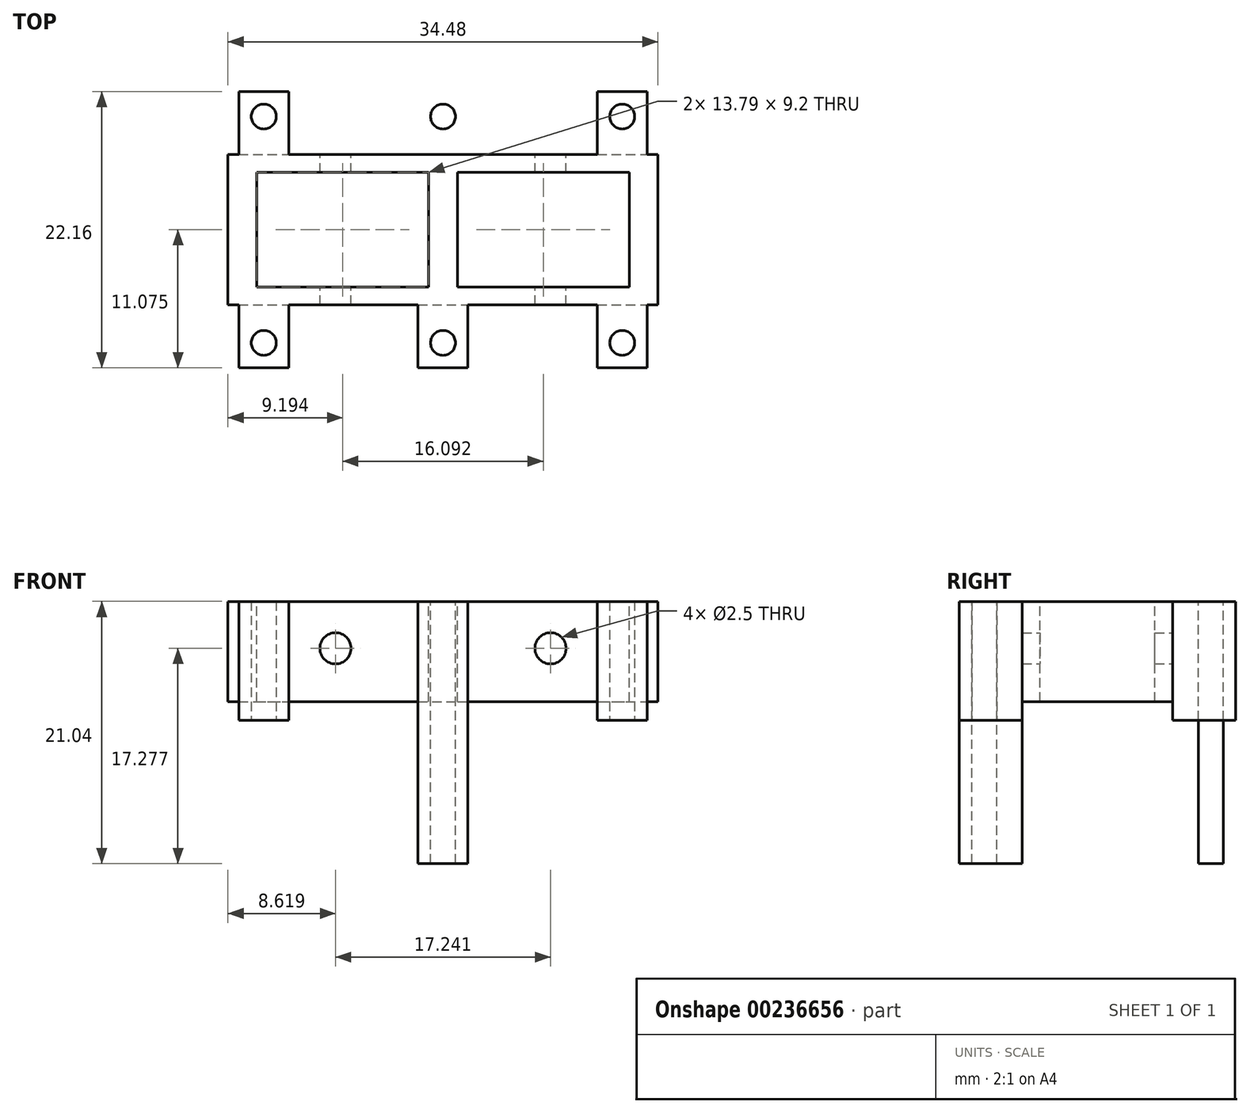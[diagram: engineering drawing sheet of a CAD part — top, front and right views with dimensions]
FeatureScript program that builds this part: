
annotation { "Feature Type Name" : "Feature", "Feature Type Description" : "" }
export const myFeature = defineFeature(function(context is Context, id is Id, definition is map)
    precondition{}
    {
        {
            assignVariable(context, id + "F0", {"name" : "scale", "anyValue" : 1 / 87});
        }
        {
            var Q0;
            Q0=qCreatedBy(makeId("Front.planeOp"),FACE);
            var sketch = newSketch(context, id + "F1", { "sketchPlane" : qUnion([Q0])});
            skLineSegment(sketch, "E0", {"start": v(0, 0) * mm, "end": v(17.24, 0) * mm});
            skLineSegment(sketch, "E1", {"start": v(17.24, 0) * mm, "end": v(17.24, 1.72) * mm});
            skLineSegment(sketch, "E2", {"start": v(17.24, 8.05) * mm, "end": v(0, 8.05) * mm});
            skLineSegment(sketch, "E3", {"start": v(0, 8.05) * mm, "end": v(0, 0) * mm, "construction": true});
            skLineSegment(sketch, "E4", {"start": v(14.37, 1.72) * mm, "end": v(14.37, 0) * mm, "construction": true});
            skLineSegment(sketch, "E5", {"start": v(0, -1.5) * mm, "end": v(17.24, -1.5) * mm, "construction": true});
            skLineSegment(sketch, "E6", {"start": v(17.24, -1.5) * mm, "end": v(17.24, 0) * mm, "construction": true});
            skLineSegment(sketch, "E7", {"start": v(17.24, 1.72) * mm, "end": v(0, 1.72) * mm, "construction": true});
            skCircle(sketch, "E8", {"center": v(8.62, 4.29) * mm, "radius": 5.78 * mm, "construction": true});
            skPoint(sketch, "E9", {"position": v(8.62, 1.72) * mm});
            skPoint(sketch, "E10.MirrorP", {"position": v(-8.62, 1.72) * mm});
            skLineSegment(sketch, "E11.MirrorCS", {"start": v(0, 0) * mm, "end": v(-17.24, 0) * mm});
            skCircle(sketch, "E12.MirrorC", {"center": v(-8.62, 4.29) * mm, "radius": 5.78 * mm, "construction": true});
            skLineSegment(sketch, "E13.MirrorCS", {"start": v(-14.37, 1.72) * mm, "end": v(-14.37, 0) * mm, "construction": true});
            skLineSegment(sketch, "E14.MirrorCS", {"start": v(-17.24, -1.5) * mm, "end": v(-17.24, 0) * mm, "construction": true});
            skLineSegment(sketch, "E15.MirrorCS", {"start": v(-17.24, 0) * mm, "end": v(-17.24, 1.72) * mm});
            skLineSegment(sketch, "E16.MirrorCS", {"start": v(-17.24, 8.05) * mm, "end": v(0, 8.05) * mm});
            skLineSegment(sketch, "E17.MirrorCS", {"start": v(0, -1.5) * mm, "end": v(-17.24, -1.5) * mm, "construction": true});
            skLineSegment(sketch, "E18.MirrorCS", {"start": v(-17.24, 1.72) * mm, "end": v(0, 1.72) * mm, "construction": true});
            skCircle(sketch, "E19", {"center": v(8.62, 4.29) * mm, "radius": 1.25 * mm});
            skCircle(sketch, "E20", {"center": v(-8.62, 4.29) * mm, "radius": 1.25 * mm});
            skLineSegment(sketch, "E21", {"start": v(17.24, 1.72) * mm, "end": v(17.24, 8.05) * mm});
            skLineSegment(sketch, "E22", {"start": v(-17.24, 8.05) * mm, "end": v(-17.24, 1.72) * mm});
            skSolve(sketch);
        }
        {
            var Q0;
            Q0=qSketchRegion(id+"F1",true);
            extrude(context, id + "F2", {"entities" : qUnion([Q0]), "depth" : (1050 * getVariable(context, 'scale')) * mm});
        }
        {
            var Q0;
            Q0=makeQuery(id+"F2.opExtrude","SWEPT_FACE",FACE,{"disambiguationData":[OSD([sQuery(id+"F1.wireOp",EDGE,"E2"),sQuery(id+"F1.wireOp",EDGE,"E16.MirrorCS")])]});
            var sketch = newSketch(context, id + "F3", { "sketchPlane" : qUnion([Q0])});
            skLineSegment(sketch, "E23.bottom", {"start": v(-17.24, 0) * mm, "end": v(17.24, 0) * mm, "construction": true});
            skLineSegment(sketch, "E23.top", {"start": v(-17.24, -12.07) * mm, "end": v(17.24, -12.07) * mm, "construction": true});
            skLineSegment(sketch, "E23.left", {"start": v(-17.24, 0) * mm, "end": v(-17.24, -12.07) * mm, "construction": true});
            skLineSegment(sketch, "E23.right", {"start": v(17.24, 0) * mm, "end": v(17.24, -12.07) * mm, "construction": true});
            skLineSegment(sketch, "E24", {"start": v(-17.24, -1.44) * mm, "end": v(17.24, -1.44) * mm, "construction": true});
            skLineSegment(sketch, "E25", {"start": v(17.24, -1.44) * mm, "end": v(17.24, -10.63) * mm, "construction": true});
            skLineSegment(sketch, "E26", {"start": v(17.24, -10.63) * mm, "end": v(-17.24, -10.63) * mm, "construction": true});
            skLineSegment(sketch, "E27", {"start": v(-14.94, 0) * mm, "end": v(-14.94, -12.07) * mm, "construction": true});
            skLineSegment(sketch, "E28", {"start": v(14.94, 0) * mm, "end": v(14.94, -12.07) * mm, "construction": true});
            skLineSegment(sketch, "E29", {"start": v(-14.94, -1.44) * mm, "end": v(-1.15, -1.44) * mm});
            skLineSegment(sketch, "E30", {"start": v(-1.15, -1.44) * mm, "end": v(-1.15, -10.63) * mm});
            skLineSegment(sketch, "E31", {"start": v(-1.15, -10.63) * mm, "end": v(-14.94, -10.63) * mm});
            skLineSegment(sketch, "E32", {"start": v(-14.94, -10.63) * mm, "end": v(-14.94, -1.44) * mm});
            skLineSegment(sketch, "E33", {"start": v(1.15, -1.44) * mm, "end": v(14.94, -1.44) * mm});
            skLineSegment(sketch, "E34", {"start": v(14.94, -1.44) * mm, "end": v(14.94, -10.63) * mm});
            skLineSegment(sketch, "E35", {"start": v(14.94, -10.63) * mm, "end": v(1.15, -10.63) * mm});
            skLineSegment(sketch, "E36", {"start": v(0, 0) * mm, "end": v(0, -12.07) * mm, "construction": true});
            skLineSegment(sketch, "E37", {"start": v(1.15, -1.44) * mm, "end": v(1.15, -10.63) * mm});
            skLineSegment(sketch, "E38", {"start": v(1.15, -6.03) * mm, "end": v(-1.15, -6.03) * mm, "construction": true});
            skPoint(sketch, "E39", {"position": v(0, -6.03) * mm});
            skSolve(sketch);
        }
        {
            var Q0;
            Q0=qSketchRegion(id+"F3",true);
            extrude(context, id + "F4", {"entities" : qUnion([Q0]), "operationType" : NewBodyOperationType.REMOVE, "endBound" : BoundingType.THROUGH_ALL, "oppositeDirection" : true, "depth" : 25 * mm});
        }
        {
            var Q0;
            Q0=makeQuery(id+"F2.opExtrude","SWEPT_FACE",FACE,{"disambiguationData":[OSD([sQuery(id+"F1.wireOp",EDGE,"E0"),sQuery(id+"F1.wireOp",EDGE,"E11.MirrorCS")])]});
            var sketch = newSketch(context, id + "F5", { "sketchPlane" : qUnion([Q0])});
            skLineSegment(sketch, "E40.bottom", {"start": v(-50, 10.92) * mm, "end": v(50, 10.92) * mm, "construction": true});
            skLineSegment(sketch, "E40.top", {"start": v(-50, 1.15) * mm, "end": v(50, 1.15) * mm, "construction": true});
            skLineSegment(sketch, "E40.left", {"start": v(-50, 10.92) * mm, "end": v(-50, 1.15) * mm, "construction": true});
            skLineSegment(sketch, "E40.right", {"start": v(50, 10.92) * mm, "end": v(50, 1.15) * mm, "construction": true});
            skPoint(sketch, "E40.middle", {"position": v(0, 6.03) * mm});
            skPoint(sketch, "E40.middle.positionSnap0", {"position": v(1.15, 6.03) * mm});
            skPoint(sketch, "E40.centerSnap0", {"position": v(1.15, 6.03) * mm});
            skCircle(sketch, "E41", {"center": v(-14.37, 15.11) * mm, "radius": 4.2 * mm, "construction": true});
            skCircle(sketch, "E42", {"center": v(14.37, 15.11) * mm, "radius": 4.2 * mm, "construction": true});
            skCircle(sketch, "E43", {"center": v(-14.37, -3.05) * mm, "radius": 4.2 * mm, "construction": true});
            skCircle(sketch, "E44", {"center": v(14.37, -3.05) * mm, "radius": 4.2 * mm, "construction": true});
            skLineSegment(sketch, "E45", {"start": v(14.37, 15.11) * mm, "end": v(-14.37, 15.11) * mm, "construction": true});
            skLineSegment(sketch, "E46", {"start": v(-14.37, -3.05) * mm, "end": v(-14.37, 15.11) * mm, "construction": true});
            skLineSegment(sketch, "E47", {"start": v(14.37, 15.11) * mm, "end": v(14.37, -3.05) * mm, "construction": true});
            skLineSegment(sketch, "E48", {"start": v(-14.37, -3.05) * mm, "end": v(14.37, -3.05) * mm, "construction": true});
            skLineSegment(sketch, "E49", {"start": v(0, 15.11) * mm, "end": v(0, -3.05) * mm, "construction": true});
            skCircle(sketch, "E50", {"center": v(-14.37, -3.05) * mm, "radius": 1 * mm});
            skLineSegment(sketch, "E51", {"start": v(-17.24, 6.03) * mm, "end": v(17.24, 6.03) * mm, "construction": true});
            skLineSegment(sketch, "E52.MirrorCS", {"start": v(14.37, -3.05) * mm, "end": v(-14.37, -3.05) * mm, "construction": true});
            skCircle(sketch, "E53.MirrorC", {"center": v(14.37, -3.05) * mm, "radius": 1 * mm});
            skCircle(sketch, "E54.MirrorC", {"center": v(-14.37, 15.11) * mm, "radius": 1 * mm});
            skCircle(sketch, "E55.MirrorC", {"center": v(14.37, 15.11) * mm, "radius": 1 * mm});
            skLineSegment(sketch, "E56.bottom", {"start": v(-16.37, 12.07) * mm, "end": v(-12.37, 12.07) * mm});
            skLineSegment(sketch, "E56.top", {"start": v(-16.37, 17.11) * mm, "end": v(-12.37, 17.11) * mm});
            skLineSegment(sketch, "E56.left", {"start": v(-16.37, 12.07) * mm, "end": v(-16.37, 17.11) * mm});
            skLineSegment(sketch, "E56.right", {"start": v(-12.37, 12.07) * mm, "end": v(-12.37, 17.11) * mm});
            skPoint(sketch, "E57", {"position": v(-14.37, 12.07) * mm});
            skLineSegment(sketch, "E58.bottom", {"start": v(12.37, 12.07) * mm, "end": v(16.37, 12.07) * mm});
            skLineSegment(sketch, "E58.top", {"start": v(12.37, 17.11) * mm, "end": v(16.37, 17.11) * mm});
            skLineSegment(sketch, "E58.left", {"start": v(12.37, 12.07) * mm, "end": v(12.37, 17.11) * mm});
            skLineSegment(sketch, "E58.right", {"start": v(16.37, 12.07) * mm, "end": v(16.37, 17.11) * mm});
            skPoint(sketch, "E59", {"position": v(14.37, 12.07) * mm});
            skLineSegment(sketch, "E60.MirrorCS", {"start": v(-16.37, 0) * mm, "end": v(-16.37, -5.05) * mm});
            skLineSegment(sketch, "E61.MirrorCS", {"start": v(-16.37, 0) * mm, "end": v(-12.37, 0) * mm});
            skLineSegment(sketch, "E62.MirrorCS", {"start": v(-12.37, 0) * mm, "end": v(-12.37, -5.05) * mm});
            skLineSegment(sketch, "E63.MirrorCS", {"start": v(-16.37, -5.05) * mm, "end": v(-12.37, -5.05) * mm});
            skLineSegment(sketch, "E64.MirrorCS", {"start": v(12.37, 0) * mm, "end": v(16.37, 0) * mm});
            skLineSegment(sketch, "E65.MirrorCS", {"start": v(12.37, 0) * mm, "end": v(12.37, -5.05) * mm});
            skLineSegment(sketch, "E66.MirrorCS", {"start": v(12.37, -5.05) * mm, "end": v(16.37, -5.05) * mm});
            skLineSegment(sketch, "E67.MirrorCS", {"start": v(16.37, 0) * mm, "end": v(16.37, -5.05) * mm});
            skSolve(sketch);
        }
        {
            var Q0;
            Q0=qSketchRegion(id+"F5",true);
            var Q1;
            Q1=qConstructionFilter(qBodyType(qCreatedBy(id+"F5",EDGE),BodyType.WIRE),ConstructionObject.NO);
            var Q2;
            Q2=makeQuery(id+"F2.opExtrude","SWEPT_FACE",FACE,{"disambiguationData":[OSD([sQuery(id+"F1.wireOp",EDGE,"E2"),sQuery(id+"F1.wireOp",EDGE,"E16.MirrorCS")])]});
            extrude(context, id + "F6", {"entities" : qUnion([Q0]), "operationType" : NewBodyOperationType.ADD, "surfaceEntities" : qUnion([Q1]), "endBound" : BoundingType.UP_TO_SURFACE, "oppositeDirection" : true, "endBoundEntityFace" : qUnion([Q2]), "depth" : 25 * mm, "hasSecondDirection" : true, "secondDirectionOppositeDirection" : false, "secondDirectionDepth" : (130 * getVariable(context, 'scale')) * mm});
        }
        {
            var Q0;
            Q0=makeQuery(id+"F2.opExtrude","SWEPT_FACE",FACE,{"disambiguationData":[OSD([sQuery(id+"F1.wireOp",EDGE,"E0"),sQuery(id+"F1.wireOp",EDGE,"E11.MirrorCS")])]});
            var sketch = newSketch(context, id + "F7", { "sketchPlane" : qUnion([Q0])});
            skPoint(sketch, "E68", {"position": v(16.8, 12.07) * mm});
            skLineSegment(sketch, "E69", {"start": v(-17.24, 6.03) * mm, "end": v(17.24, 6.03) * mm, "construction": true});
            skCircle(sketch, "E70", {"center": v(-14.37, 15.11) * mm, "radius": 1 * mm, "construction": true});
            skCircle(sketch, "E71", {"center": v(14.37, 15.11) * mm, "radius": 1 * mm, "construction": true});
            skLineSegment(sketch, "E72", {"start": v(14.37, 15.11) * mm, "end": v(-14.37, 15.11) * mm, "construction": true});
            skCircle(sketch, "E73", {"center": v(0, 15.11) * mm, "radius": 1 * mm});
            skCircle(sketch, "E74.MirrorC", {"center": v(0, -3.05) * mm, "radius": 1 * mm});
            skPoint(sketch, "E75.MirrorP", {"position": v(16.8, 0) * mm});
            skLineSegment(sketch, "E76", {"start": v(0, 15.11) * mm, "end": v(0, -3.05) * mm, "construction": true});
            skLineSegment(sketch, "E77.bottom", {"start": v(-2, 12.07) * mm, "end": v(2, 12.07) * mm});
            skLineSegment(sketch, "E77.top", {"start": v(-2, 17.11) * mm, "end": v(2, 17.11) * mm});
            skLineSegment(sketch, "E77.left", {"start": v(-2, 12.07) * mm, "end": v(-2, 17.11) * mm});
            skLineSegment(sketch, "E77.right", {"start": v(2, 12.07) * mm, "end": v(2, 17.11) * mm});
            skPoint(sketch, "E78", {"position": v(0, 12.07) * mm});
            skLineSegment(sketch, "E79.MirrorCS", {"start": v(2, 0) * mm, "end": v(2, -5.05) * mm});
            skLineSegment(sketch, "E80.MirrorCS", {"start": v(-2, 0) * mm, "end": v(2, 0) * mm});
            skLineSegment(sketch, "E81.MirrorCS", {"start": v(-2, -5.05) * mm, "end": v(2, -5.05) * mm});
            skLineSegment(sketch, "E82.MirrorCS", {"start": v(-2, 0) * mm, "end": v(-2, -5.05) * mm});
            skSolve(sketch);
        }
        {
            var Q0;
            Q0=makeQuery(id+"F7.imprint","IMPRINT",FACE,{"disambiguationData":[TD([[makeQuery(id+"F7.imprint","IMPRINT",EDGE,{"derivedFrom":sQuery(id+"F7.wireOp",EDGE,"E73")}),-1.0]])]});
            var Q1;
            Q1=makeQuery(id+"F7.imprint","IMPRINT",FACE,{"disambiguationData":[TD([[makeQuery(id+"F7.imprint","IMPRINT",EDGE,{"derivedFrom":sQuery(id+"F7.wireOp",EDGE,"E74.MirrorC")}),1.0]])]});
            var Q2;
            {var subQ0=sQuery(id+"F1.wireOp",EDGE,"E16.MirrorCS");var subQ1=sQuery(id+"F1.wireOp",EDGE,"E2");Q2=makeQuery(id+"F6.boolean.opBoolean","MERGE",FACE,{"derivedFrom":[makeQuery(id+"F2.opExtrude","SWEPT_FACE",FACE,{"disambiguationData":[OSD([subQ1,subQ0])]}),makeQuery(id+"F6.opExtrude","CAP_FACE",FACE,{"disambiguationData":[OSD([subQ1,subQ0]),ownerDisambiguation([makeQuery(id+"F6.opExtrude","SWEPT_BODY",BODY,{"disambiguationData":[OSD([sQuery(id+"F5.wireOp",EDGE,"E50"),sQuery(id+"F5.wireOp",EDGE,"260c3738-1ddf-4a0d-a3f6-4ed18a3080593.MirrorCS"),sQuery(id+"F5.wireOp",EDGE,"260c3738-1ddf-4a0d-a3f6-4ed18a3080594.MirrorCS"),sQuery(id+"F5.wireOp",EDGE,"260c3738-1ddf-4a0d-a3f6-4ed18a30805913.MirrorCS"),sQuery(id+"F5.wireOp",EDGE,"260c3738-1ddf-4a0d-a3f6-4ed18a30805914.MirrorCS")])]})])],"isStart":false}),makeQuery(id+"F6.opExtrude","CAP_FACE",FACE,{"disambiguationData":[OSD([subQ1,subQ0]),ownerDisambiguation([makeQuery(id+"F6.opExtrude","SWEPT_BODY",BODY,{"disambiguationData":[OSD([sQuery(id+"F5.wireOp",EDGE,"NGU8r28S-R4YQ-ClXm-H3s3-VvEhc2yyaSJW"),sQuery(id+"F5.wireOp",EDGE,"rEJE2d4l-dEjL-jT7w-uFwG-o0KEyOl6WYqS.bottom"),sQuery(id+"F5.wireOp",EDGE,"rEJE2d4l-dEjL-jT7w-uFwG-o0KEyOl6WYqS.top"),sQuery(id+"F5.wireOp",EDGE,"rEJE2d4l-dEjL-jT7w-uFwG-o0KEyOl6WYqS.left"),sQuery(id+"F5.wireOp",EDGE,"rEJE2d4l-dEjL-jT7w-uFwG-o0KEyOl6WYqS.right")])]})])],"isStart":false}),makeQuery(id+"F6.opExtrude","CAP_FACE",FACE,{"disambiguationData":[OSD([subQ1,subQ0]),ownerDisambiguation([makeQuery(id+"F6.opExtrude","SWEPT_BODY",BODY,{"disambiguationData":[OSD([sQuery(id+"F5.wireOp",EDGE,"WqDLV06R-3XXb-Ktht-Y2sh-0tFAFLF6ySSx"),sQuery(id+"F5.wireOp",EDGE,"c1b8ae5c-8274-4790-a20f-2bbc2f58163d3.MirrorCS"),sQuery(id+"F5.wireOp",EDGE,"c1b8ae5c-8274-4790-a20f-2bbc2f58163d4.MirrorCS"),sQuery(id+"F5.wireOp",EDGE,"c1b8ae5c-8274-4790-a20f-2bbc2f58163d5.MirrorCS"),sQuery(id+"F5.wireOp",EDGE,"c1b8ae5c-8274-4790-a20f-2bbc2f58163d6.MirrorCS")])]})])],"isStart":false}),makeQuery(id+"F6.opExtrude","CAP_FACE",FACE,{"disambiguationData":[OSD([subQ1,subQ0]),ownerDisambiguation([makeQuery(id+"F6.opExtrude","SWEPT_BODY",BODY,{"disambiguationData":[OSD([sQuery(id+"F5.wireOp",EDGE,"260c3738-1ddf-4a0d-a3f6-4ed18a3080590.MirrorC"),sQuery(id+"F5.wireOp",EDGE,"260c3738-1ddf-4a0d-a3f6-4ed18a3080591.MirrorCS"),sQuery(id+"F5.wireOp",EDGE,"260c3738-1ddf-4a0d-a3f6-4ed18a3080592.MirrorCS"),sQuery(id+"F5.wireOp",EDGE,"260c3738-1ddf-4a0d-a3f6-4ed18a30805911.MirrorCS"),sQuery(id+"F5.wireOp",EDGE,"260c3738-1ddf-4a0d-a3f6-4ed18a30805912.MirrorCS")])]})])],"isStart":false})]});}
            var Q3;
            {var subQ0=sQuery(id+"F1.wireOp",EDGE,"E16.MirrorCS");var subQ1=sQuery(id+"F1.wireOp",EDGE,"E2");Q3=makeQuery(id+"F6.boolean.opBoolean","MERGE",FACE,{"derivedFrom":[makeQuery(id+"F2.opExtrude","SWEPT_FACE",FACE,{"disambiguationData":[OSD([subQ1,subQ0])]}),makeQuery(id+"F6.opExtrude","CAP_FACE",FACE,{"disambiguationData":[OSD([subQ1,subQ0]),ownerDisambiguation([makeQuery(id+"F6.opExtrude","SWEPT_BODY",BODY,{"disambiguationData":[OSD([sQuery(id+"F5.wireOp",EDGE,"E54.MirrorC"),sQuery(id+"F5.wireOp",EDGE,"4zQsxl9Z-I2SQ-CTgq-iFO3-FLsdcYwDSmnR.bottom"),sQuery(id+"F5.wireOp",EDGE,"4zQsxl9Z-I2SQ-CTgq-iFO3-FLsdcYwDSmnR.top"),sQuery(id+"F5.wireOp",EDGE,"4zQsxl9Z-I2SQ-CTgq-iFO3-FLsdcYwDSmnR.left"),sQuery(id+"F5.wireOp",EDGE,"4zQsxl9Z-I2SQ-CTgq-iFO3-FLsdcYwDSmnR.right")])]})])],"isStart":false}),makeQuery(id+"F6.opExtrude","CAP_FACE",FACE,{"disambiguationData":[OSD([subQ1,subQ0]),ownerDisambiguation([makeQuery(id+"F6.opExtrude","SWEPT_BODY",BODY,{"disambiguationData":[OSD([sQuery(id+"F5.wireOp",EDGE,"E55.MirrorC"),sQuery(id+"F5.wireOp",EDGE,"XAPZbS1x-Wh9E-NJBz-62o6-e6b0lxS2XX1N.bottom"),sQuery(id+"F5.wireOp",EDGE,"XAPZbS1x-Wh9E-NJBz-62o6-e6b0lxS2XX1N.left"),sQuery(id+"F5.wireOp",EDGE,"XAPZbS1x-Wh9E-NJBz-62o6-e6b0lxS2XX1N.right"),sQuery(id+"F5.wireOp",EDGE,"ceUdVZib-BXrb-NKpS-qx1A-vHXEwOxlMTEA")])]})])],"isStart":false}),makeQuery(id+"F6.opExtrude","CAP_FACE",FACE,{"disambiguationData":[OSD([subQ1,subQ0]),ownerDisambiguation([makeQuery(id+"F6.opExtrude","SWEPT_BODY",BODY,{"disambiguationData":[OSD([sQuery(id+"F5.wireOp",EDGE,"E50"),sQuery(id+"F5.wireOp",EDGE,"8480fd8e-db6f-478a-b294-a8017d5093d64.MirrorCS"),sQuery(id+"F5.wireOp",EDGE,"8480fd8e-db6f-478a-b294-a8017d5093d65.MirrorCS"),sQuery(id+"F5.wireOp",EDGE,"8480fd8e-db6f-478a-b294-a8017d5093d67.MirrorCS"),sQuery(id+"F5.wireOp",EDGE,"d969c6aa-171a-4fa7-9cbf-224d25e09a050.MirrorCS")])]})])],"isStart":false}),makeQuery(id+"F6.opExtrude","CAP_FACE",FACE,{"disambiguationData":[OSD([subQ1,subQ0]),ownerDisambiguation([makeQuery(id+"F6.opExtrude","SWEPT_BODY",BODY,{"disambiguationData":[OSD([sQuery(id+"F5.wireOp",EDGE,"8480fd8e-db6f-478a-b294-a8017d5093d63.MirrorCS"),sQuery(id+"F5.wireOp",EDGE,"E53.MirrorC"),sQuery(id+"F5.wireOp",EDGE,"8480fd8e-db6f-478a-b294-a8017d5093d610.MirrorCS"),sQuery(id+"F5.wireOp",EDGE,"8480fd8e-db6f-478a-b294-a8017d5093d614.MirrorCS"),sQuery(id+"F5.wireOp",EDGE,"8480fd8e-db6f-478a-b294-a8017d5093d616.MirrorCS")])]})])],"isStart":false})]});}
            extrude(context, id + "F8", {"entities" : qUnion([Q0, Q1]), "operationType" : NewBodyOperationType.ADD, "endBoundEntityFace" : qUnion([Q2]), "depth" : (130 + 1000) * getVariable(context, 'scale') * mm, "hasSecondDirection" : true, "secondDirectionBound" : SecondDirectionBoundingType.UP_TO_SURFACE, "secondDirectionOppositeDirection" : true, "secondDirectionBoundEntityFace" : qUnion([Q3]), "secondDirectionDepth" : (130 + 1000) * getVariable(context, 'scale') * mm});
        }
    });
